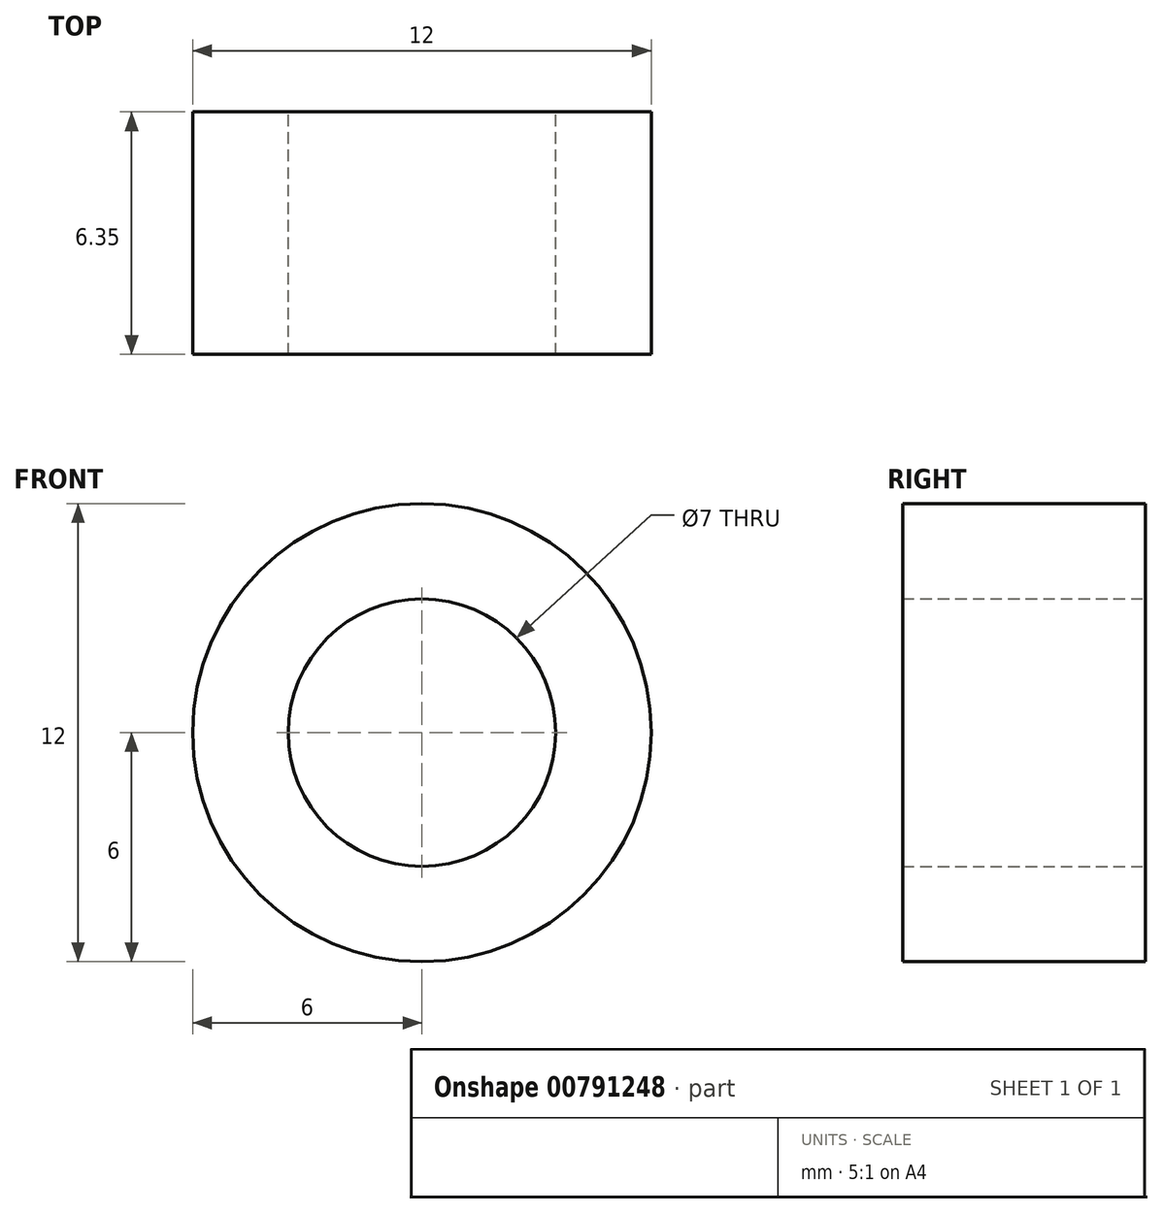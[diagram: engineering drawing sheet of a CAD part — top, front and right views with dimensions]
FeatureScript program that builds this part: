
annotation { "Feature Type Name" : "Feature", "Feature Type Description" : "" }
export const myFeature = defineFeature(function(context is Context, id is Id, definition is map)
    precondition{}
    {
        {
            var Q0;
            Q0=qCreatedBy(makeId("Front.planeOp"),FACE);
            var sketch = newSketch(context, id + "F0", { "sketchPlane" : qUnion([Q0])});
            skCircle(sketch, "E0", {"center": v(0, 0) * mm, "radius": 3.5 * mm});
            skCircle(sketch, "E1", {"center": v(0, 0) * mm, "radius": 6 * mm});
            skSolve(sketch);
        }
        {
            var Q0;
            Q0=qSketchRegion(id+"F0",true);
            extrude(context, id + "F1", {"entities" : qUnion([Q0]), "depth" : 6.35 * mm, "offsetDistance" : 25 * mm});
        }
    });
